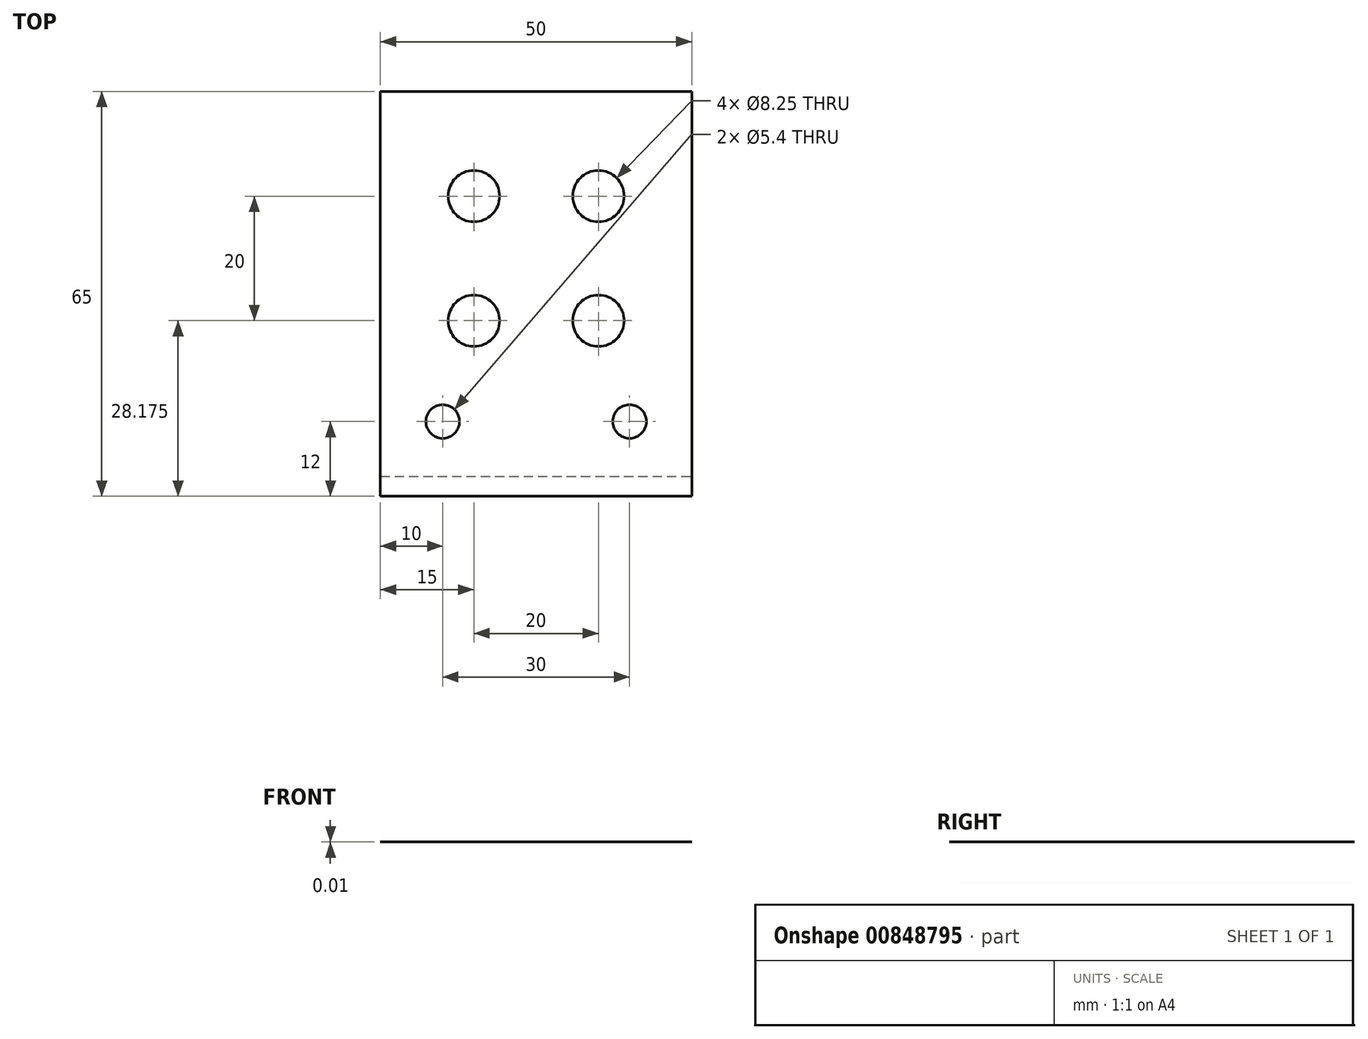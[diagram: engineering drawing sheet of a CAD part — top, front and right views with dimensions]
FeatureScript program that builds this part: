
annotation { "Feature Type Name" : "Feature", "Feature Type Description" : "" }
export const myFeature = defineFeature(function(context is Context, id is Id, definition is map)
    precondition{}
    {
        {
            var Q0;
            Q0=qCreatedBy(makeId("Top.planeOp"),FACE);
            var sketch = newSketch(context, id + "F0", { "sketchPlane" : qUnion([Q0])});
            skLineSegment(sketch, "E0.bottom", {"start": v(25, -32.5) * mm, "end": v(-25, -32.5) * mm});
            skLineSegment(sketch, "E0.top", {"start": v(25, 32.5) * mm, "end": v(-25, 32.5) * mm});
            skLineSegment(sketch, "E0.left", {"start": v(25, -32.5) * mm, "end": v(25, 32.5) * mm});
            skLineSegment(sketch, "E0.right", {"start": v(-25, -32.5) * mm, "end": v(-25, 32.5) * mm});
            skPoint(sketch, "E0.middle", {"position": v(0, 0) * mm});
            skSolve(sketch);
        }
        {
            var Q0;
            Q0=makeQuery(id+"F0.imprint","IMPRINT",FACE,{"disambiguationData":[TD([[makeQuery(id+"F0.imprint","IMPRINT",EDGE,{"derivedFrom":sQuery(id+"F0.wireOp",EDGE,"E0.bottom")}),-1.0]])]});
            extrude(context, id + "F1", {"entities" : qUnion([Q0]), "depth" : 3 / 203.2 * mm, "offsetDistance" : 25 * mm});
        }
        {
            var Q0;
            Q0=makeQuery(id+"F1.opExtrude","CAP_FACE",FACE,{"disambiguationData":[OSD([sQuery(id+"F0.wireOp",EDGE,"E0.bottom"),sQuery(id+"F0.wireOp",EDGE,"E0.top"),sQuery(id+"F0.wireOp",EDGE,"E0.left"),sQuery(id+"F0.wireOp",EDGE,"E0.right")])],"isStart":true});
            var sketch = newSketch(context, id + "F2", { "sketchPlane" : qUnion([Q0])});
            skLineSegment(sketch, "E1.bottom", {"start": v(-25, -32.5) * mm, "end": v(25, -32.5) * mm});
            skLineSegment(sketch, "E1.top", {"start": v(-25, 29.33) * mm, "end": v(25, 29.33) * mm});
            skLineSegment(sketch, "E1.left", {"start": v(-25, -32.5) * mm, "end": v(-25, 29.33) * mm});
            skLineSegment(sketch, "E1.right", {"start": v(25, -32.5) * mm, "end": v(25, 29.33) * mm});
            skSolve(sketch);
        }
        {
            var Q0;
            Q0=makeQuery(id+"F2.imprint","IMPRINT",FACE,{"disambiguationData":[TD([[makeQuery(id+"F2.imprint","IMPRINT",EDGE,{"derivedFrom":sQuery(id+"F2.wireOp",EDGE,"E1.bottom")}),-1.0]])]});
            extrude(context, id + "F3", {"entities" : qUnion([Q0]), "operationType" : NewBodyOperationType.REMOVE, "oppositeDirection" : true, "depth" : 1 / 203.2 * mm, "offsetDistance" : 25 * mm});
        }
        {
            var Q0;
            Q0=makeQuery(id+"F1.opExtrude","CAP_FACE",FACE,{"disambiguationData":[OSD([sQuery(id+"F0.wireOp",EDGE,"E0.bottom"),sQuery(id+"F0.wireOp",EDGE,"E0.top"),sQuery(id+"F0.wireOp",EDGE,"E0.left"),sQuery(id+"F0.wireOp",EDGE,"E0.right")])],"isStart":false});
            var sketch = newSketch(context, id + "F4", { "sketchPlane" : qUnion([Q0])});
            skPoint(sketch, "E2.MirrorP", {"position": v(-10, -4.33) * mm});
            skPoint(sketch, "E3", {"position": v(-10, 15.67) * mm});
            skPoint(sketch, "E4.MirrorP", {"position": v(10, 15.67) * mm});
            skPoint(sketch, "E5.MirrorP", {"position": v(10, -4.33) * mm});
            skSolve(sketch);
        }
        {
            var Q0;
            Q0=sQuery(id+"F4.wireOp",VERTEX,"E3");
            var Q1;
            Q1=sQuery(id+"F4.wireOp",VERTEX,"E4.MirrorP");
            var Q2;
            Q2=sQuery(id+"F4.wireOp",VERTEX,"E5.MirrorP");
            var Q3;
            Q3=sQuery(id+"F4.wireOp",VERTEX,"E2.MirrorP");
            var Q4;
            Q4=makeQuery(id+"F1.opExtrude","SWEPT_BODY",BODY,{"disambiguationData":[OSD([sQuery(id+"F0.wireOp",EDGE,"E0.bottom"),sQuery(id+"F0.wireOp",EDGE,"E0.top"),sQuery(id+"F0.wireOp",EDGE,"E0.left"),sQuery(id+"F0.wireOp",EDGE,"E0.right")])]});
            hole(context, id + "F5", {"style" : HoleStyle.C_BORE, "endStyle" : HoleEndStyle.THROUGH, "standardTappedOrClearance" : lookupTablePath({ "fit" : "Normal", "standard" : "ISO", "size" : "M4", "type" : "Clearance" }), "standardBlindInLast" : lookupTablePath({ "fit" : "Standard", "standard" : "ISO", "size" : "M4", "type" : "Clearance" }), "holeDiameter" : 4.4 * mm, "cBoreDiameter" : 8.25 * mm, "cBoreDepth" : 4 * mm, "majorDiameter" : 5 * mm, "isTappedThrough" : true, "tappedDepth" : 7.9 * mm, "tapClearance" : 3, "startFromSketch" : true, "locations" : qUnion([Q0, Q1, Q2, Q3]), "scope" : qUnion([Q4])});
        }
        {
            var Q0;
            Q0=makeQuery(id+"F1.opExtrude","CAP_FACE",FACE,{"disambiguationData":[OSD([sQuery(id+"F0.wireOp",EDGE,"E0.bottom"),sQuery(id+"F0.wireOp",EDGE,"E0.top"),sQuery(id+"F0.wireOp",EDGE,"E0.left"),sQuery(id+"F0.wireOp",EDGE,"E0.right")])],"isStart":false});
            var sketch = newSketch(context, id + "F6", { "sketchPlane" : qUnion([Q0])});
            skPoint(sketch, "E6", {"position": v(-15, -20.5) * mm});
            skPoint(sketch, "E7.MirrorP", {"position": v(15, -20.5) * mm});
            skSolve(sketch);
        }
        {
            var Q0;
            Q0=sQuery(id+"F6.wireOp",VERTEX,"E6");
            var Q1;
            Q1=sQuery(id+"F6.wireOp",VERTEX,"E7.MirrorP");
            var Q2;
            Q2=makeQuery(id+"F1.opExtrude","SWEPT_BODY",BODY,{"disambiguationData":[OSD([sQuery(id+"F0.wireOp",EDGE,"E0.bottom"),sQuery(id+"F0.wireOp",EDGE,"E0.top"),sQuery(id+"F0.wireOp",EDGE,"E0.left"),sQuery(id+"F0.wireOp",EDGE,"E0.right")])]});
            hole(context, id + "F7", {"style" : HoleStyle.SIMPLE, "endStyle" : HoleEndStyle.THROUGH, "standardTappedOrClearance" : lookupTablePath({ "standard" : "ISO", "engagement" : "50%", "pitch" : "1 mm", "size" : "M6", "type" : "Tapped" }), "standardBlindInLast" : lookupTablePath({ "standard" : "ISO", "engagement" : "50%", "pitch" : "1 mm", "size" : "M6", "type" : "Tapped" }), "holeDiameter" : 5.4 * mm, "majorDiameter" : 6 * mm, "showTappedDepth" : true, "isTappedThrough" : true, "tappedDepth" : 2 * mm, "tapClearance" : 3, "startFromSketch" : true, "locations" : qUnion([Q0, Q1]), "scope" : qUnion([Q2])});
        }
    });
